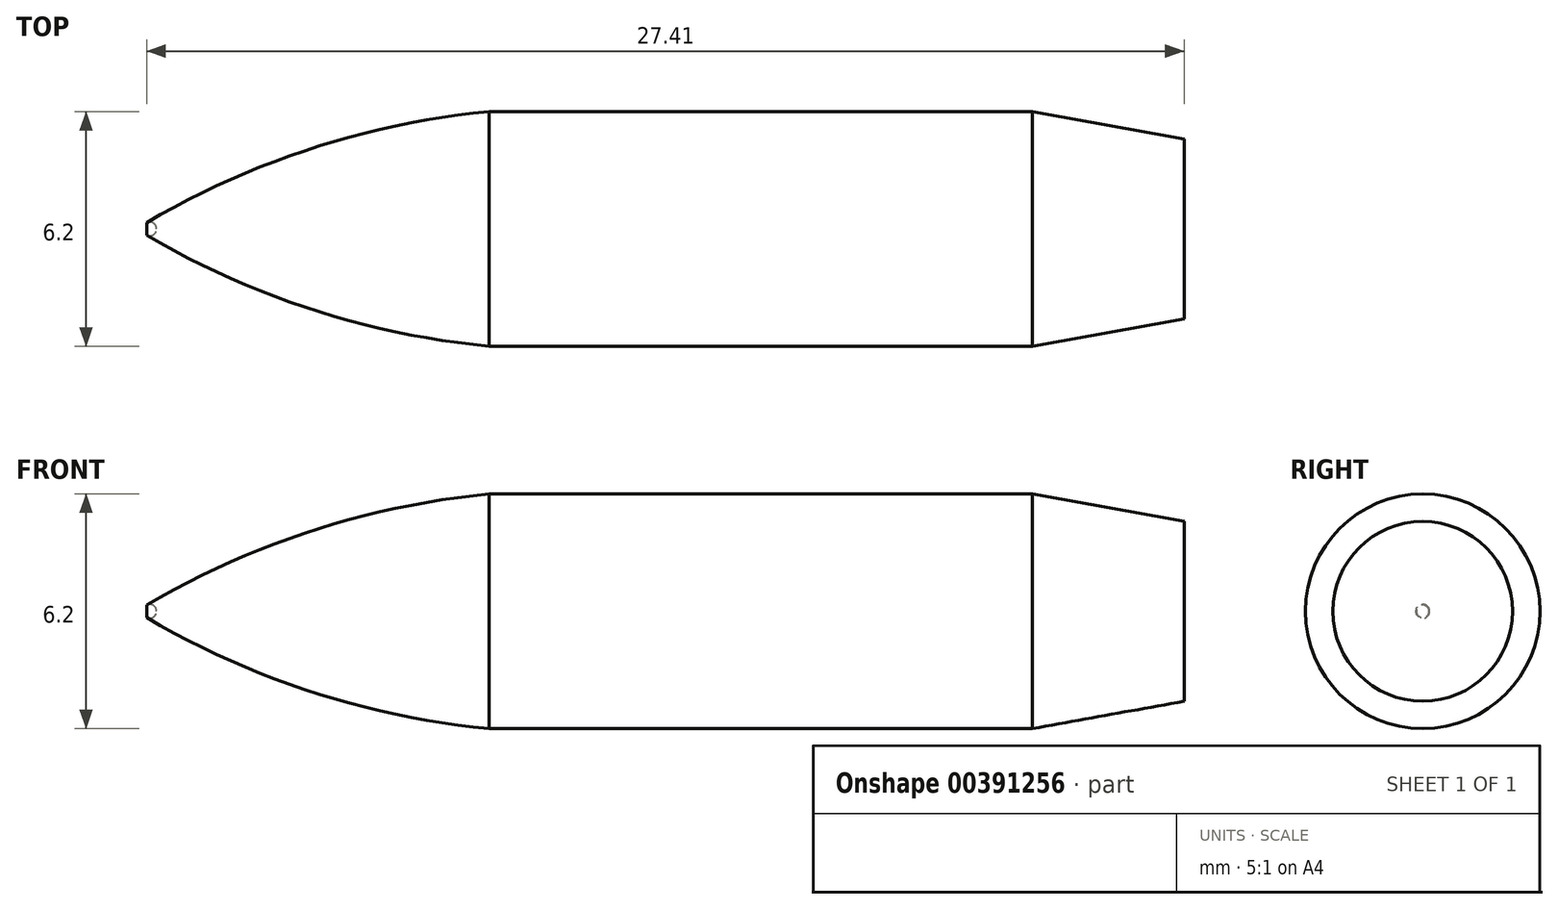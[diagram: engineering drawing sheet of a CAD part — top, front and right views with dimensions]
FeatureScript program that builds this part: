
annotation { "Feature Type Name" : "Feature", "Feature Type Description" : "" }
export const myFeature = defineFeature(function(context is Context, id is Id, definition is map)
    precondition{}
    {
        {
            var Q0;
            Q0=qCreatedBy(makeId("Front.planeOp"),FACE);
            var sketch = newSketch(context, id + "F0", { "sketchPlane" : qUnion([Q0])});
            skLineSegment(sketch, "E0", {"start": v(0, 0) * mm, "end": v(0, 2.37) * mm});
            skLineSegment(sketch, "E1", {"start": v(0, 2.37) * mm, "end": v(-4.01, 3.1) * mm});
            skLineSegment(sketch, "E2", {"start": v(-4.01, 3.1) * mm, "end": v(-18.36, 3.1) * mm});
            skArc(sketch, "E3", {"start": v(-18.36, 3.1) * mm, "mid": v(-23.06, 2.12) * mm, "end": v(-27.44, 0.15) * mm});
            skLineSegment(sketch, "E4", {"start": v(0, 0) * mm, "end": v(-27.46, 0) * mm});
            skLineSegment(sketch, "E5", {"start": v(-27.46, 0) * mm, "end": v(-27.33, 0) * mm});
            skCircle(sketch, "E6", {"center": v(-27.33, 0) * mm, "radius": 0.18 * mm});
            skSolve(sketch);
        }
        {
            var Q0;
            {var subQ4=sQuery(id+"F0.wireOp",EDGE,"E0");Q0=makeQuery(id+"F0.imprint","IMPRINT",FACE,{"disambiguationData":[TD([[makeQuery(id+"F0.imprint","IMPRINT",EDGE,{"derivedFrom":subQ4}),1.0]])]});}
            var Q1;
            Q1=sQuery(id+"F0.wireOp",EDGE,"E4");
            revolve(context, id + "F1", {"entities" : qUnion([Q0]), "axis" : qUnion([Q1]), "revolveType" : RevolveType.FULL});
        }
    });
